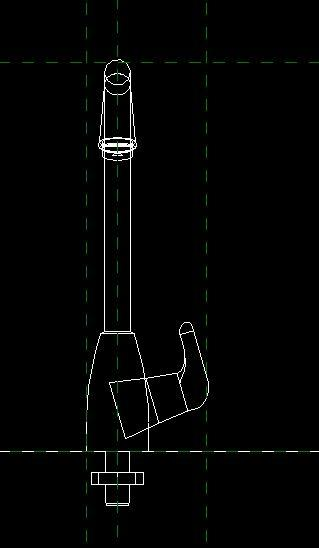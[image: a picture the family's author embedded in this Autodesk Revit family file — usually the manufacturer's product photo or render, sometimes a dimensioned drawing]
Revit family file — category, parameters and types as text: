
# Revit family: TT5015551-Griferia-Lavaplatos-Monocontrol-Tanta
name_source: partatom
category: Plumbing Fixtures
units: mm (PartAtom-declared; Revit-internal decimal feet)

## family parameters
Cut with Voids When Loaded = No
Host = Face
OmniClass Number = 23.31.11.00
Part Type = Normal
Room Calculation Point = No
Round Connector Dimension = Use Diameter
Shared = No

## types (1)
- TT5015551-Griferia-Lavaplatos-Monocontrol-Tanta
    Alto = 395 mm  [stored 1.29593 ft]
    Ancho = 77 mm  [stored 0.252625 ft]
    Capacidad de flujo máximo a 60 psi = 8,3 L/min
    Creado por = IDD
    Default Elevation = 1219 mm
    Fabricante = Corona
    Fecha de creación = 11/08/2020
    Garantia = 30 años
    Garantía Acabados = 2 años
    Material = Corona_Plastico_Cromado
    Peso  Bruto = 1,950 gr / 4,30 lb
    Peso Neto = 1,760 gr / 3,88 lb
    Profundidad = 200 mm  [stored 0.656168 ft]
    Temperatura de uso = 5ºC a 71ºC
    Vida útil o desgaste (pico) = 50.000 ciclos
    Vida útil o desgaste (unidad) = 500.000 ciclos

note: [stored X ft] marks values corroborated as IEEE doubles in the binary element streams (Revit-internal decimal feet)

## geometry (parser evidence)
native form markers: Sweep x10
no freeform markers — native parametric forms only
